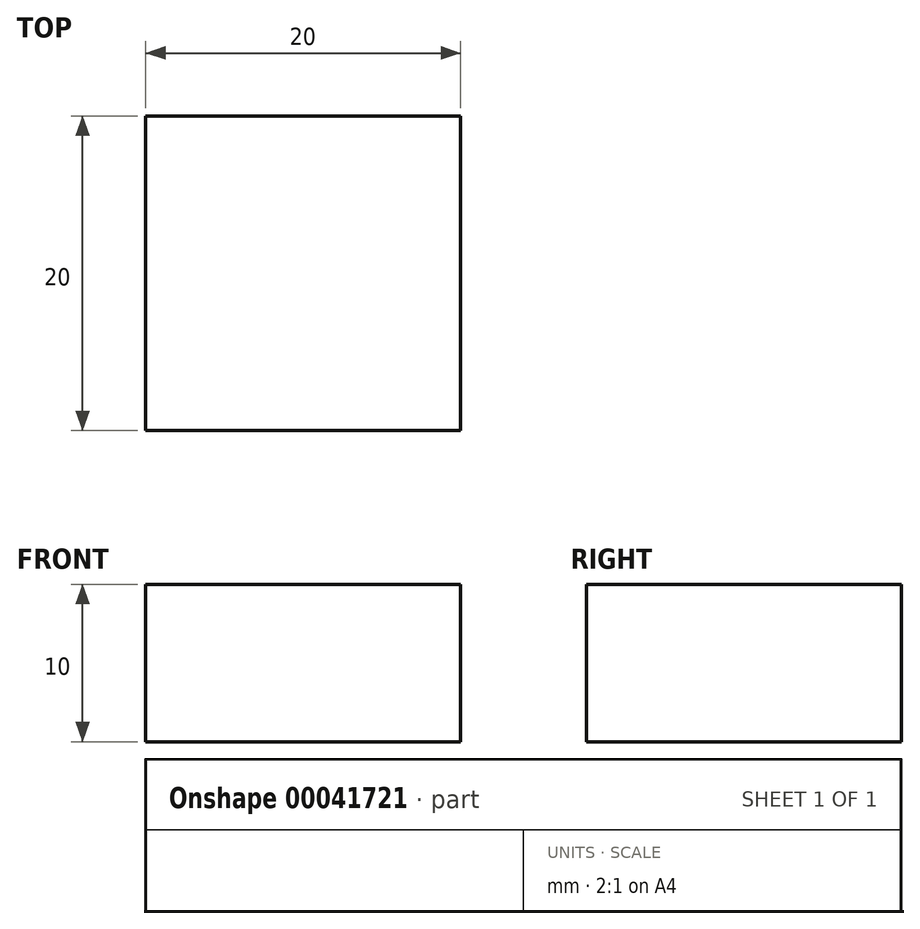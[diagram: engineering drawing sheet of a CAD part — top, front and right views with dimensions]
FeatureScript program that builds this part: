
annotation { "Feature Type Name" : "Feature", "Feature Type Description" : "" }
export const myFeature = defineFeature(function(context is Context, id is Id, definition is map)
    precondition{}
    {
        {
            var Q0;
            Q0=qCreatedBy(makeId("Top.planeOp"),FACE);
            var sketch = newSketch(context, id + "F0", { "sketchPlane" : qUnion([Q0])});
            skLineSegment(sketch, "E0.rect.bottom", {"start": v(10, -10) * mm, "end": v(-10, -10) * mm});
            skLineSegment(sketch, "E0.rect.top", {"start": v(10, 10) * mm, "end": v(-10, 10) * mm});
            skLineSegment(sketch, "E0.rect.left", {"start": v(10, -10) * mm, "end": v(10, 10) * mm});
            skLineSegment(sketch, "E0.rect.right", {"start": v(-10, -10) * mm, "end": v(-10, 10) * mm});
            skPoint(sketch, "E0.rect.middle", {"position": v(0, 0) * mm});
            skSolve(sketch);
        }
        {
            var Q0;
            Q0=makeQuery(id+"F0.imprint","IMPRINT",FACE,{"disambiguationData":[TD([[makeQuery(id+"F0.imprint","IMPRINT",EDGE,{"derivedFrom":sQuery(id+"F0.wireOp",EDGE,"E0.rect.bottom")}),-1.0]])]});
            extrude(context, id + "F1", {"entities" : qUnion([Q0]), "depth" : 10 * mm});
        }
    });
